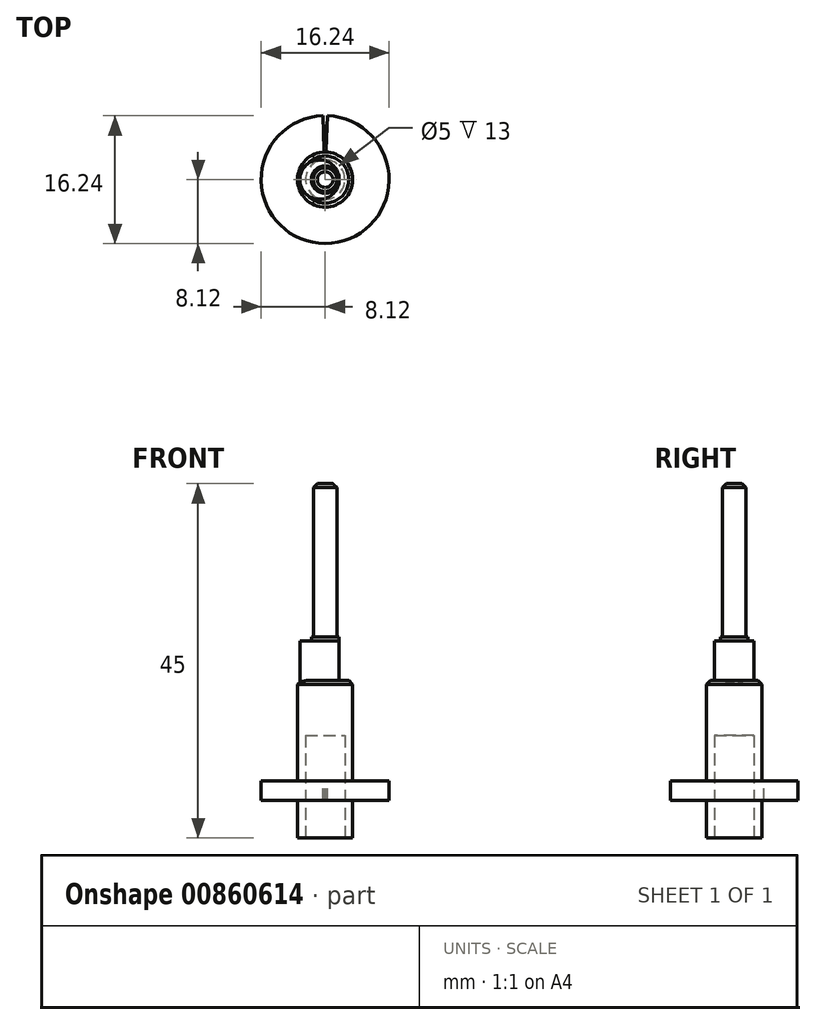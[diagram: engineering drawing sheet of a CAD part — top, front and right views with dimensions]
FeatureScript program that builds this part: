
annotation { "Feature Type Name" : "Feature", "Feature Type Description" : "" }
export const myFeature = defineFeature(function(context is Context, id is Id, definition is map)
    precondition{}
    {
        {
            var Q0;
            Q0=qCreatedBy(makeId("Top.planeOp"),FACE);
            var sketch = newSketch(context, id + "F0", { "sketchPlane" : qUnion([Q0])});
            skCircle(sketch, "E0", {"center": v(0, 0) * mm, "radius": 1.5 * mm});
            skSolve(sketch);
        }
        {
            var Q0;
            Q0 = qSketchRegion(id + "F0", true);
            extrude(context, id + "F1", {"entities" : qUnion([Q0]), "depth" : 25 * mm, "offsetDistance" : 25 * mm});
        }
        {
            var Q0;
            Q0=makeQuery(id+"F1.opExtrude","CAP_FACE",FACE,{"disambiguationData":[OSD([sQuery(id+"F0.wireOp",EDGE,"E0")])],"isStart":true});
            var sketch = newSketch(context, id + "F2", { "sketchPlane" : qUnion([Q0])});
            skCircle(sketch, "E1", {"center": v(-0.71, 0) * mm, "radius": 2.5 * mm});
            skLineSegment(sketch, "E2", {"start": v(-0.71, 0) * mm, "end": v(0, 0) * mm, "construction": true});
            skSolve(sketch);
        }
        {
            var Q0;
            Q0 = qSketchRegion(id + "F2", true);
            extrude(context, id + "F3", {"entities" : qUnion([Q0]), "operationType" : NewBodyOperationType.ADD, "oppositeDirection" : true, "depth" : 5 * mm, "offsetDistance" : 25 * mm});
        }
        {
            var Q0;
            Q0=makeQuery(id+"F3.opExtrude","CAP_FACE",FACE,{"disambiguationData":[OSD([sQuery(id+"F2.wireOp",EDGE,"E1")])],"isStart":false});
            var sketch = newSketch(context, id + "F4", { "sketchPlane" : qUnion([Q0])});
            skCircle(sketch, "E3", {"center": v(0, 0) * mm, "radius": 1.75 * mm});
            skSolve(sketch);
        }
        {
            var Q0;
            Q0 = qSketchRegion(id + "F4", true);
            extrude(context, id + "F5", {"entities" : qUnion([Q0]), "operationType" : NewBodyOperationType.ADD, "depth" : .5 * mm, "offsetDistance" : 25 * mm});
        }
        {
            var Q0;
            Q0=makeQuery(id+"F3.boolean.opBoolean","MERGE",FACE,{"derivedFrom":[makeQuery(id+"F1.opExtrude","CAP_FACE",FACE,{"disambiguationData":[OSD([sQuery(id+"F0.wireOp",EDGE,"E0")])],"isStart":true}),makeQuery(id+"F3.opExtrude","CAP_FACE",FACE,{"disambiguationData":[OSD([sQuery(id+"F2.wireOp",EDGE,"E1")])],"isStart":true})]});
            var sketch = newSketch(context, id + "F6", { "sketchPlane" : qUnion([Q0])});
            skCircle(sketch, "E4", {"center": v(0, 0) * mm, "radius": 3.5 * mm});
            skSolve(sketch);
        }
        {
            var Q0;
            Q0 = qSketchRegion(id + "F6", true);
            extrude(context, id + "F7", {"entities" : qUnion([Q0]), "operationType" : NewBodyOperationType.ADD, "depth" : 20 * mm, "offsetDistance" : 25 * mm});
        }
        {
            var Q0;
            Q0=qCreatedBy(makeId("Front.planeOp"),FACE);
            var sketch = newSketch(context, id + "F8", { "sketchPlane" : qUnion([Q0])});
            skLineSegment(sketch, "E5.bottom", {"start": v(0, -15.25) * mm, "end": v(8.12, -15.25) * mm});
            skLineSegment(sketch, "E5.top", {"start": v(0, -12.75) * mm, "end": v(8.12, -12.75) * mm});
            skLineSegment(sketch, "E5.left", {"start": v(0, -12.75) * mm, "end": v(0, -15.25) * mm});
            skLineSegment(sketch, "E5.right", {"start": v(8.12, -12.75) * mm, "end": v(8.12, -15.25) * mm});
            skPoint(sketch, "E6", {"position": v(0, -14) * mm});
            skLineSegment(sketch, "E7", {"start": v(0, 0) * mm, "end": v(0, -21.72) * mm, "construction": true});
            skSolve(sketch);
        }
        {
            var Q0;
            Q0 = qSketchRegion(id + "F8", true);
            var Q1;
            Q1=sQuery(id+"F8.wireOp",EDGE,"E7");
            revolve(context, id + "F9", {"operationType" : NewBodyOperationType.ADD, "surfaceOperationType" : NewSurfaceOperationType.NEW, "entities" : qUnion([Q0]), "axis" : qUnion([Q1]), "revolveType" : RevolveType.FULL});
        }
        {
            var Q0;
            Q0=makeQuery(id+"F7.opExtrude","CAP_FACE",FACE,{"disambiguationData":[OSD([sQuery(id+"F6.wireOp",EDGE,"E4")])],"isStart":false});
            var sketch = newSketch(context, id + "F10", { "sketchPlane" : qUnion([Q0])});
            skCircle(sketch, "E8", {"center": v(0, 0) * mm, "radius": 2.5 * mm});
            skSolve(sketch);
        }
        {
            var Q0;
            Q0 = qSketchRegion(id + "F10", true);
            extrude(context, id + "F11", {"entities" : qUnion([Q0]), "operationType" : NewBodyOperationType.REMOVE, "oppositeDirection" : true, "depth" : 13 * mm, "offsetDistance" : 25 * mm});
        }
        {
            var Q0;
            Q0=makeQuery(id+"F1.opExtrude","CAP_EDGE",EDGE,{"disambiguationData":[OSD([sQuery(id+"F0.wireOp",EDGE,"E0")])],"isStart":false});
            var Q1;
            Q1=makeQuery(id+"F11.boolean.opBoolean","COPY",EDGE,{"derivedFrom":makeQuery(id+"F11.opExtrude","CAP_EDGE",EDGE,{"disambiguationData":[OSD([sQuery(id+"F10.wireOp",EDGE,"E8")])],"isStart":true})});
            var Q2;
            Q2=makeQuery(id+"F7.opExtrude","CAP_EDGE",EDGE,{"disambiguationData":[OSD([sQuery(id+"F6.wireOp",EDGE,"E4")])],"isStart":true});
            chamfer(context, id + "F12", {"entities" : qUnion([Q0, Q1, Q2]), "width" : .5 * mm, "tangentPropagation" : true});
        }
        {
            var Q0;
            Q0=makeQuery(id+"F9.opRevolve","SWEPT_FACE",FACE,{"disambiguationData":[OSD([sQuery(id+"F8.wireOp",EDGE,"E5.top")])]});
            var sketch = newSketch(context, id + "F13", { "sketchPlane" : qUnion([Q0])});
            skLineSegment(sketch, "E9", {"start": v(0, 0) * mm, "end": v(0, 8.12) * mm, "construction": true});
            skLineSegment(sketch, "E10", {"start": v(0, 0) * mm, "end": v(0.28, 8.12) * mm, "construction": true});
            skLineSegment(sketch, "E11.MirrorCS", {"start": v(0, 0) * mm, "end": v(-0.28, 8.12) * mm, "construction": true});
            skArc(sketch, "E12", {"start": v(-0.13, 3.75) * mm, "mid": v(0, 3.75) * mm, "end": v(0.13, 3.75) * mm});
            skArc(sketch, "E13", {"start": v(-0.28, 8.12) * mm, "mid": v(0, 8.12) * mm, "end": v(0.28, 8.12) * mm});
            skLineSegment(sketch, "E14", {"start": v(-0.13, 3.75) * mm, "end": v(-0.28, 8.12) * mm});
            skLineSegment(sketch, "E15", {"start": v(0.13, 3.75) * mm, "end": v(0.28, 8.12) * mm});
            skSolve(sketch);
        }
        {
            var Q0;
            Q0 = qSketchRegion(id + "F13", true);
            extrude(context, id + "F14", {"entities" : qUnion([Q0]), "operationType" : NewBodyOperationType.REMOVE, "endBound" : BoundingType.THROUGH_ALL, "oppositeDirection" : true, "depth" : 25 * mm, "offsetDistance" : 25 * mm});
        }
    });
